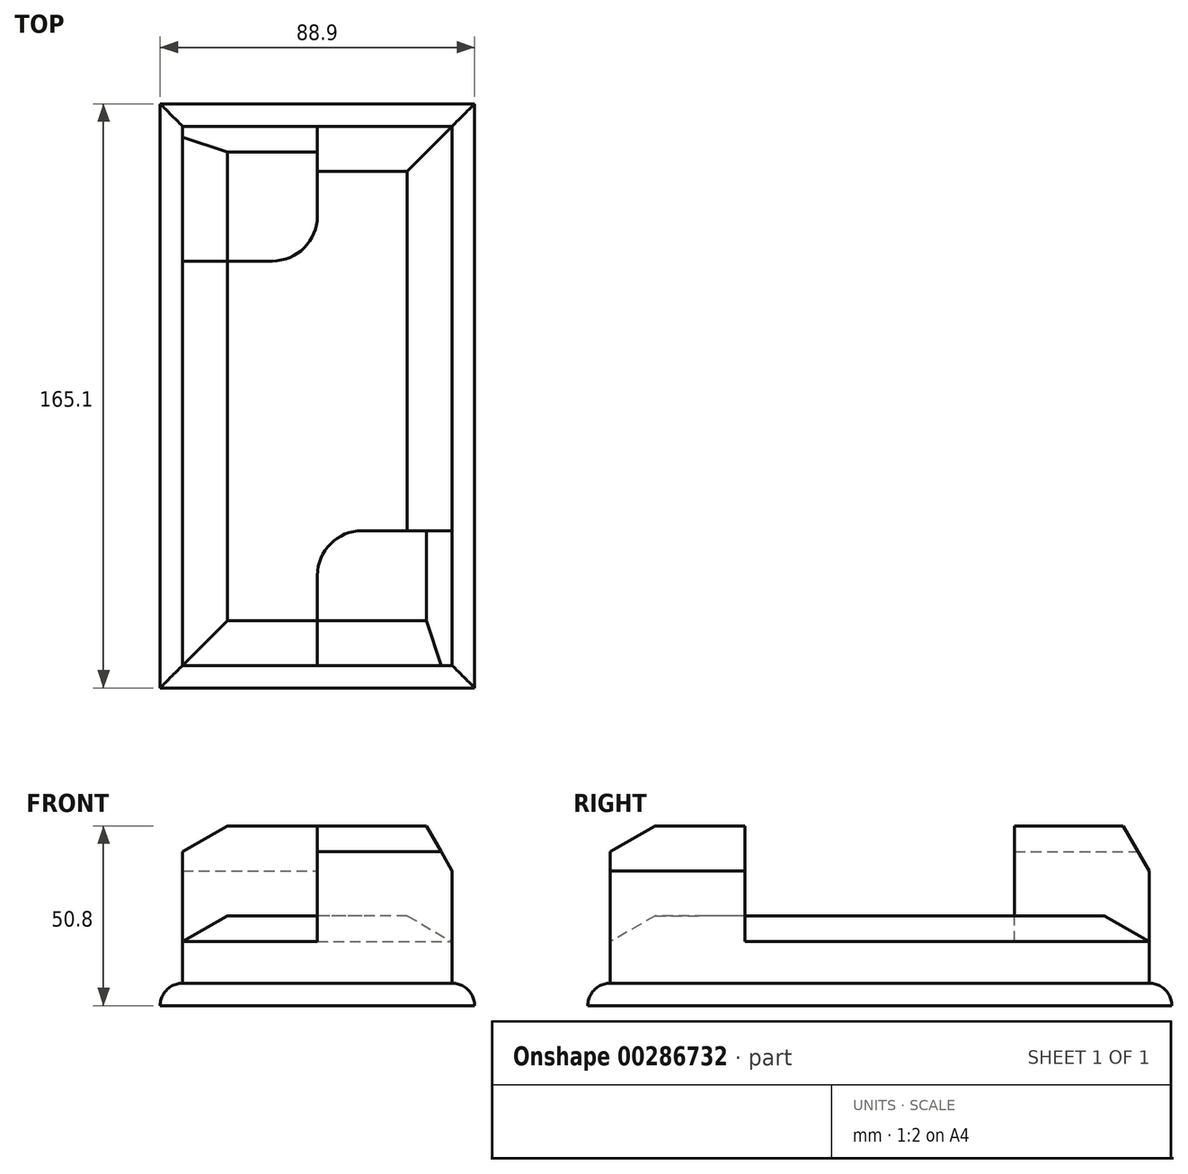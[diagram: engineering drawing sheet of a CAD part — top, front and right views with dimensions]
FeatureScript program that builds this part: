
annotation { "Feature Type Name" : "Feature", "Feature Type Description" : "" }
export const myFeature = defineFeature(function(context is Context, id is Id, definition is map)
    precondition{}
    {
        {
            var Q0;
            Q0=qCreatedBy(makeId("Top.planeOp"),FACE);
            var sketch = newSketch(context, id + "F0", { "sketchPlane" : qUnion([Q0])});
            skLineSegment(sketch, "E0.bottom", {"start": v(-38.1, 76.2) * mm, "end": v(38.1, 76.2) * mm});
            skLineSegment(sketch, "E0.top", {"start": v(-38.1, -76.2) * mm, "end": v(38.1, -76.2) * mm});
            skLineSegment(sketch, "E0.left", {"start": v(-38.1, 76.2) * mm, "end": v(-38.1, -76.2) * mm});
            skLineSegment(sketch, "E0.right", {"start": v(38.1, 76.2) * mm, "end": v(38.1, -76.2) * mm});
            skPoint(sketch, "E0.middle", {"position": v(0, 0) * mm});
            skLineSegment(sketch, "E1.0", {"start": v(-44.45, 82.55) * mm, "end": v(44.45, 82.55) * mm});
            skLineSegment(sketch, "E1.1", {"start": v(-44.45, 82.55) * mm, "end": v(-44.45, -82.55) * mm});
            skLineSegment(sketch, "E1.2", {"start": v(-44.45, -82.55) * mm, "end": v(44.45, -82.55) * mm});
            skLineSegment(sketch, "E1.3", {"start": v(44.45, 82.55) * mm, "end": v(44.45, -82.55) * mm});
            skPoint(sketch, "E2.endSnap0", {"position": v(0, 76.2) * mm});
            skLineSegment(sketch, "E3", {"start": v(0, -76.2) * mm, "end": v(0, -50.8) * mm});
            skPoint(sketch, "E3.endSnap0", {"position": v(0, -76.2) * mm});
            skPoint(sketch, "E4", {"position": v(-38.1, 0) * mm});
            skPoint(sketch, "E5", {"position": v(38.1, 0) * mm});
            skLineSegment(sketch, "E6", {"start": v(0, 76.2) * mm, "end": v(0, 50.8) * mm});
            skLineSegment(sketch, "E7", {"start": v(-12.7, 38.1) * mm, "end": v(-38.1, 38.1) * mm});
            skPoint(sketch, "E8", {"position": v(0, 38.1) * mm});
            skArc(sketch, "E9", {"start": v(-12.7, 38.1) * mm, "mid": v(-3.72, 41.82) * mm, "end": v(0, 50.8) * mm});
            skLineSegment(sketch, "E10", {"start": v(38.1, -38.1) * mm, "end": v(12.7, -38.1) * mm});
            skPoint(sketch, "E11", {"position": v(0, -38.1) * mm});
            skArc(sketch, "E12", {"start": v(12.7, -38.1) * mm, "mid": v(3.72, -41.82) * mm, "end": v(0, -50.8) * mm});
            skLineSegment(sketch, "E13", {"start": v(38.1, 76.2) * mm, "end": v(38.1, 82.55) * mm});
            skLineSegment(sketch, "E14", {"start": v(-38.1, -76.2) * mm, "end": v(-38.1, -82.55) * mm});
            skSolve(sketch);
        }
        {
            var Q0;
            {var subQ8=sQuery(id+"F0.wireOp",EDGE,"E1.1");Q0=makeQuery(id+"F0.imprint","IMPRINT",FACE,{"disambiguationData":[TD([[makeQuery(id+"F0.imprint","IMPRINT",EDGE,{"derivedFrom":subQ8}),1.0]])]});}
            var Q1;
            {var subQ7=sQuery(id+"F0.wireOp",EDGE,"E1.3");Q1=makeQuery(id+"F0.imprint","IMPRINT",FACE,{"disambiguationData":[TD([[makeQuery(id+"F0.imprint","IMPRINT",EDGE,{"derivedFrom":subQ7}),-1.0]])]});}
            extrude(context, id + "F1", {"entities" : qUnion([Q0, Q1]), "depth" : 6.35 * mm});
        }
        {
            var Q0;
            {var subQ4=sQuery(id+"F0.wireOp",EDGE,"E3");Q0=makeQuery(id+"F0.imprint","IMPRINT",FACE,{"disambiguationData":[TD([[makeQuery(id+"F0.imprint","IMPRINT",EDGE,{"derivedFrom":subQ4}),1.0]])]});}
            extrude(context, id + "F2", {"entities" : qUnion([Q0]), "operationType" : NewBodyOperationType.ADD, "depth" : 25.4 * mm});
        }
        {
            var Q0;
            {var subQ4=sQuery(id+"F0.wireOp",EDGE,"E6");Q0=makeQuery(id+"F0.imprint","IMPRINT",FACE,{"disambiguationData":[TD([[makeQuery(id+"F0.imprint","IMPRINT",EDGE,{"derivedFrom":subQ4}),-1.0]])]});}
            var Q1;
            {var subQ0=sQuery(id+"F0.wireOp",EDGE,"E3");Q1=makeQuery(id+"F0.imprint","IMPRINT",FACE,{"disambiguationData":[TD([[makeQuery(id+"F0.imprint","IMPRINT",EDGE,{"derivedFrom":subQ0}),-1.0]])]});}
            extrude(context, id + "F3", {"entities" : qUnion([Q0, Q1]), "operationType" : NewBodyOperationType.ADD, "depth" : 50.8 * mm});
        }
        {
            var Q0;
            Q0=makeQuery(id+"F2.opExtrude","CAP_EDGE",EDGE,{"disambiguationData":[OSD([sQuery(id+"F0.wireOp",EDGE,"E0.left")])],"isStart":false});
            var Q1;
            Q1=makeQuery(id+"F3.opExtrude","CAP_EDGE",EDGE,{"disambiguationData":[OSD([sQuery(id+"F0.wireOp",EDGE,"E0.left")])],"isStart":false});
            var Q2;
            Q2=makeQuery(id+"F3.opExtrude","CAP_EDGE",EDGE,{"disambiguationData":[OSD([sQuery(id+"F0.wireOp",EDGE,"E0.bottom")])],"isStart":false});
            var Q3;
            Q3=makeQuery(id+"F2.opExtrude","CAP_EDGE",EDGE,{"disambiguationData":[OSD([sQuery(id+"F0.wireOp",EDGE,"E0.bottom")])],"isStart":false});
            var Q4;
            Q4=makeQuery(id+"F2.opExtrude","CAP_EDGE",EDGE,{"disambiguationData":[OSD([sQuery(id+"F0.wireOp",EDGE,"E0.right")])],"isStart":false});
            var Q5;
            Q5=makeQuery(id+"F3.opExtrude","CAP_EDGE",EDGE,{"disambiguationData":[OSD([sQuery(id+"F0.wireOp",EDGE,"E0.right")])],"isStart":false});
            var Q6;
            Q6=makeQuery(id+"F3.opExtrude","CAP_EDGE",EDGE,{"disambiguationData":[OSD([sQuery(id+"F0.wireOp",EDGE,"E0.top")])],"isStart":false});
            var Q7;
            Q7=makeQuery(id+"F2.opExtrude","CAP_EDGE",EDGE,{"disambiguationData":[OSD([sQuery(id+"F0.wireOp",EDGE,"E0.top")])],"isStart":false});
            chamfer(context, id + "F4", {"entities" : qUnion([Q0, Q1, Q2, Q3, Q4, Q5, Q6, Q7]), "chamferType" : ChamferType.OFFSET_ANGLE, "width" : 12.7 * mm, "oppositeDirection" : false, "angle" : 30 * degree, "tangentPropagation" : true});
        }
        {
            var Q0;
            Q0=makeQuery(id+"F1.opExtrude","CAP_EDGE",EDGE,{"disambiguationData":[OSD([sQuery(id+"F0.wireOp",EDGE,"E1.1")])],"isStart":false});
            var Q1;
            Q1=makeQuery(id+"F1.opExtrude","CAP_EDGE",EDGE,{"disambiguationData":[OSD([sQuery(id+"F0.wireOp",EDGE,"E1.0")])],"isStart":false});
            var Q2;
            Q2=makeQuery(id+"F1.opExtrude","CAP_EDGE",EDGE,{"disambiguationData":[OSD([sQuery(id+"F0.wireOp",EDGE,"E1.3")])],"isStart":false});
            var Q3;
            Q3=makeQuery(id+"F1.opExtrude","CAP_EDGE",EDGE,{"disambiguationData":[OSD([sQuery(id+"F0.wireOp",EDGE,"E1.2")])],"isStart":false});
            fillet(context, id + "F5", {"entities" : qUnion([Q0, Q1, Q2, Q3]), "radius" : 6.35 * mm, "tangentPropagation" : true, "allowEdgeOverflow" : false});
        }
    });
